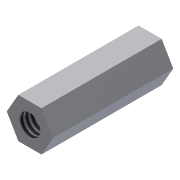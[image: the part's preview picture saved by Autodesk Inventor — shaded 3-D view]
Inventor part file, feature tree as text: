
AUTODESK INVENTOR PART (.ipt)
format: ipt  version: 2013 (Build 170138000, 138)  size: 81,408 bytes
history: native  units: in
note: dims shown in document units (in); Inventor stores cm internally (conversion verified against a paired STEP export)
features: sketch x2, extrude x1, hole x1, mirror x1
ambient origin geometry x8: Origin, YZ Plane, XZ Plane, XY Plane, X Axis, Y Axis, Z Axis, Center Point
bodies: Solid1 (feature_tree)
feature tree (5):
  extrude  "Extrusion1"  Depth=0.75in TaperAngle=0.0deg
  hole  "Hole1"  [1 undecoded]
  mirror  "Mirror1"
  sketch  "Sketch1"  dims[d0=0.25in d1=0.75in d2=0.0in]
  sketch  "Sketch2"  dims[d3=0.13in d4=0.375in d5=0.375in d6=0.25in d7=0.5635in d8=0.375in d9=0.0in]
note: 1 required parameter value undecoded (feature->parameter linkage not recoverable at this tier; creation-order binding heuristic only, values carry confidence <= 0.55)
